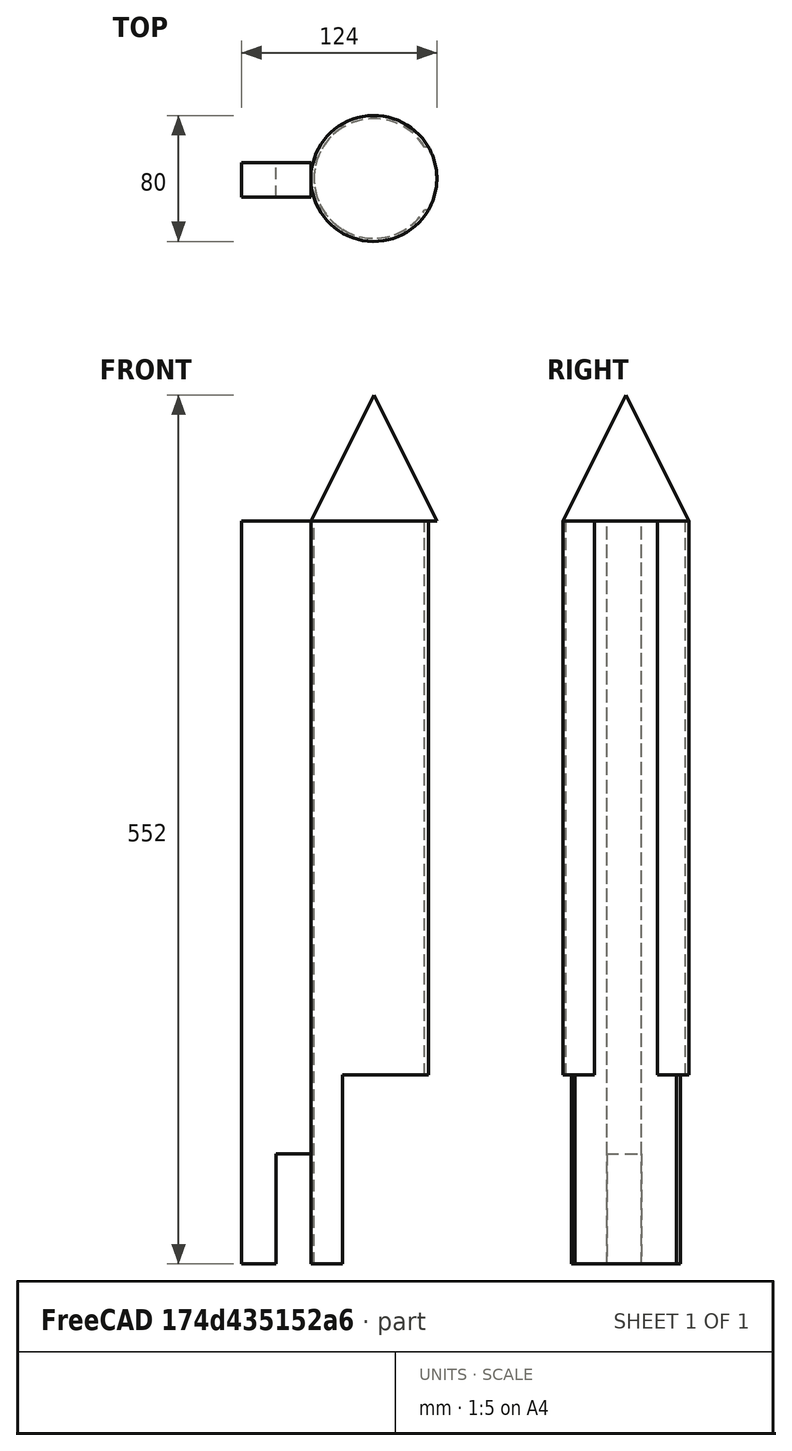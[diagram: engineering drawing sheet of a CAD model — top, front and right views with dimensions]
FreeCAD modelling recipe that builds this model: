
FCSTD DOCUMENT  (FreeCAD 0.16R6703 (Git))
Label: rocket
License: Public Domain
LicenseURL: http://en.wikipedia.org/wiki/Public_domain
objects: Part::Box×4, Part::Cut×3, Part::Cylinder×2, Part::MultiFuse×2, Part::Cone×1
note: 12 computed .brp shape members not serialized (recipe doc carries the construction recipe); baked Part::Feature solids carry a one-line shape summary decoded from their .brp

FEATURE [Part::Cylinder] Cylinder  label="rocket_cylinder_outside"
  Angle = 360
  Height = 472
  Radius = 40
FEATURE [Part::Cylinder] Cylinder001  label="rocket_cylinder_inside"
  Angle = 360
  Height = 500
  Placement = pos=(0,0,-10) rot=(0,0,1;0rad)
  Radius = 38
FEATURE [Part::Cut] Cut  label="rocket_hollow_cylinder"
  Base = -> Cylinder
  Tool = -> Cylinder001
FEATURE [Part::Box] Box  label="opening"
  Height = 120
  Length = 100
  Placement = pos=(-20,-50,0) rot=(0,0,1;0rad)
  Width = 100
FEATURE [Part::Box] Box001  label="opening2"
  Height = 472
  Length = 60
  Placement = pos=(0,-20,0) rot=(0,0,1;0rad)
  Width = 40
FEATURE [Part::MultiFuse] Fusion  label="opening_final"
  Shapes = -> [Box,Box001]
FEATURE [Part::Cut] Cut001  label="rocket_container"
  Base = -> Cut
  Tool = -> Fusion
FEATURE [Part::Cone] Cone  label="rocket_cap"
  Angle = 360
  Height = 80
  Placement = pos=(0,0,472) rot=(0,0,1;0rad)
  Radius1 = 40
  Radius2 = 0
FEATURE [Part::Box] Box002  label="holder"
  Height = 472
  Length = 44
  Placement = pos=(-84,-12,0) rot=(0,0,1;0rad)
  Width = 22
FEATURE [Part::Box] Box003  label="holder_opening"
  Height = 70
  Length = 22
  Placement = pos=(-62,-30,0) rot=(0,0,1;0rad)
  Width = 60
FEATURE [Part::Cut] Cut002  label="holder_final"
  Base = -> Box002
  Tool = -> Box003
FEATURE [Part::MultiFuse] Fusion001  label="rocket"
  Shapes = -> [Cut001,Cone,Cut002]
